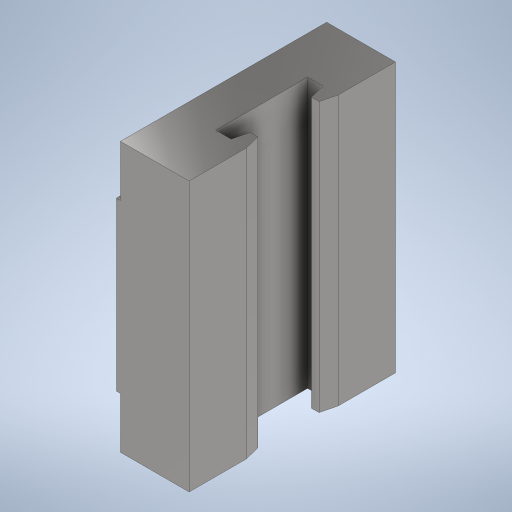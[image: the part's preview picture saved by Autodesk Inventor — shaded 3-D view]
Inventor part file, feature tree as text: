
AUTODESK INVENTOR PART (.ipt)
format: ipt  version: 2023 (Build 270158000, 158)  size: 269,824 bytes
history: native  units: mm
features: sketch x3, extrude x2, hole x1
ambient origin geometry x8: Origin, YZ Plane, XZ Plane, XY Plane, X Axis, Y Axis, Z Axis, Center Point
bodies: Solid1 (feature_tree)
feature tree (6):
  extrude  "Extrusion1"  Depth=9.5mm
  hole  "Hole1"  [1 undecoded]
  extrude  "Extrusion2"  Depth=12.0mm
  sketch  "Sketch1"  dims[d2=8.0mm d3=1.0mm d5=0.5mm d6=4.0mm d8=9.5mm]
  sketch  "Sketch2"  dims[d9=27.0mm d10=35.25mm d11=0.0mm]
  sketch  "Sketch3"  dims[d12=0.0mm d13=12.0mm d14=2.0mm d15=2.0mm d16=20.0mm d17=20.0mm d18=15.0mm d19=15.0mm d20=0.0mm d21=0.0mm d22=35.25mm d23=27.0mm d24=10.125mm d25=3.5mm d26=2.459mm d27=4.0mm d28=3.023mm d29=2.0mm d30=14.3117mm d31=5.0mm d32=20.594885mm d33=35.25mm d34=21.9mm d35=6.675mm d36=0.5mm d37=0.0mm]
note: 1 required parameter value undecoded (feature->parameter linkage not recoverable at this tier; creation-order binding heuristic only, values carry confidence <= 0.55)
